# Revit family: P400227-031
name_source: partatom
category: Lighting Fixtures
revit_build: Autodesk Revit 2014 (Build: 20130308_1515(x64)
units: mm (PartAtom-declared; Revit-internal decimal feet)

## types (1)
- P400227-031
    Apparent Load = 40 VA
    Assembly Code = D5020200
    Default Elevation = 48 "
    Description = Inspired at its roots by an understated beauty and a breathtaking formal elegance, the Bonita Collection Six-Light Satin Black Foyer Chandelier will make a stunning addition to any luxurious living space. Narrow drum shades circle the structure's center as they are held in place by black candlestick light bases supported by elegantly curved arms. A round, shiny base serves as a decorative foundation for the light fixture.
    Features = Round, shiny base serves as a decorative base for the foyer light.
Handsome black central column stretches from the light fixture's base to the ceiling.
Black candlestick light bases supported by elegantly curved arms hold the drum shades in place.
Ideal for any foyer, entryway, or kitchen.
Elegant choice for modern, luxury, or transitional interiors.
Measures 30-1/2-inch width by 24-inch height.
Uses six candelabra base bulbs that are sold separately (40w max - LED or incandescent).
Able to be fully dimmable with dimmable bulbs.
Includes installation instructions and mounting hardware.
Progress Lighting products are designed for exceptional quality, reliability, and functionality.
    Fixture distribution = Direct
    Glass = Paint - Hubbell - White Texture
    Gold = Hubbell - Gold
    Height = 11 "
    Housing Material = Paint - Hubbell - Textured Camera Black
    Lamp = LED or Medium Base
    Load Classification = Lighting
    Manufacturer = Progress Lighting
    Model = P400227-031
    Power Factor = 1
    Product Documentation Link = https://hubbellcdn.com
    Product Link = https://www.hubbell.com
    Square = 6 "
    URL = https://www.hubbell.com
    Voltage = 120 V
    Warranty = 1 year Warranty
    Wattage Comments = 40W
    Watts = 40 W

## geometry (parser evidence)
native form markers: Sweep x6
no freeform markers — native parametric forms only
